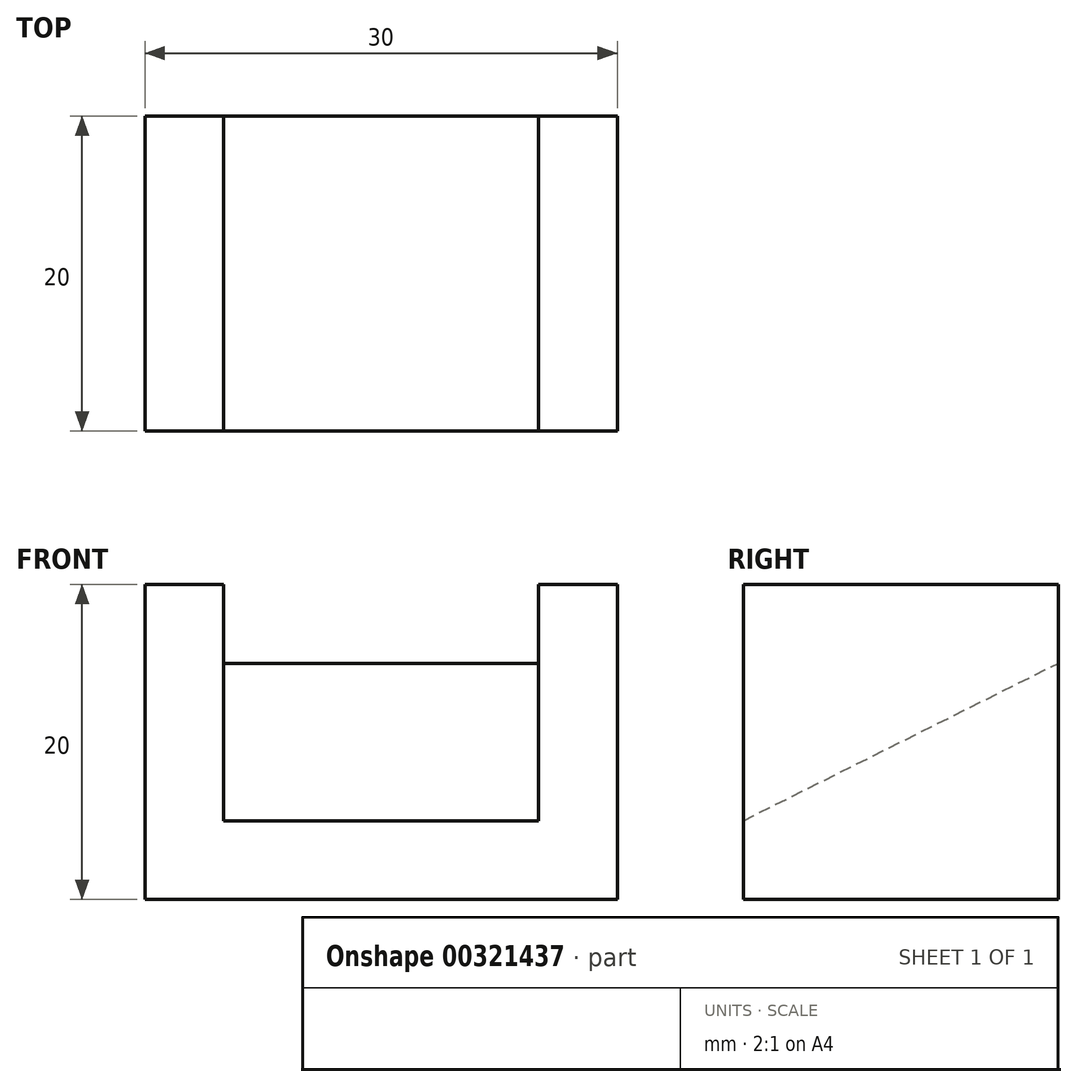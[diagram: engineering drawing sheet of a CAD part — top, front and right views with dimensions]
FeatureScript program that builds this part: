
annotation { "Feature Type Name" : "Feature", "Feature Type Description" : "" }
export const myFeature = defineFeature(function(context is Context, id is Id, definition is map)
    precondition{}
    {
        {
            var Q0;
            Q0=qCreatedBy(makeId("Front.planeOp"),FACE);
            var sketch = newSketch(context, id + "F0", { "sketchPlane" : qUnion([Q0])});
            skLineSegment(sketch, "E0.bottom", {"start": v(0, 0) * mm, "end": v(20, 0) * mm});
            skLineSegment(sketch, "E0.top", {"start": v(0, 15) * mm, "end": v(20, 15) * mm});
            skLineSegment(sketch, "E0.left", {"start": v(0, 0) * mm, "end": v(0, 15) * mm});
            skLineSegment(sketch, "E0.right", {"start": v(20, 0) * mm, "end": v(20, 15) * mm});
            skSolve(sketch);
        }
        {
            var Q0;
            Q0 = qSketchRegion(id + "F0", true);
            extrude(context, id + "F1", {"entities" : qUnion([Q0]), "depth" : 20 * mm});
        }
        {
            var Q0;
            Q0=qCreatedBy(makeId("Right.planeOp"),FACE);
            var sketch = newSketch(context, id + "F2", { "sketchPlane" : qUnion([Q0])});
            skLineSegment(sketch, "E1", {"start": v(-20, 15) * mm, "end": v(-20, 5) * mm});
            skLineSegment(sketch, "E2", {"start": v(-20, 5) * mm, "end": v(0, 15) * mm});
            skLineSegment(sketch, "E3", {"start": v(0, 15) * mm, "end": v(-20, 15) * mm});
            skSolve(sketch);
        }
        {
            var Q0;
            Q0 = qSketchRegion(id + "F2", true);
            extrude(context, id + "F3", {"entities" : qUnion([Q0]), "operationType" : NewBodyOperationType.REMOVE, "endBound" : BoundingType.THROUGH_ALL, "depth" : 25 * mm});
        }
        {
            var Q0;
            Q0=makeQuery(id+"F1.opExtrude","SWEPT_FACE",FACE,{"disambiguationData":[OSD([sQuery(id+"F0.wireOp",EDGE,"E0.right")])]});
            var sketch = newSketch(context, id + "F4", { "sketchPlane" : qUnion([Q0])});
            skLineSegment(sketch, "E4.bottom", {"start": v(0, 0) * mm, "end": v(-20, 0) * mm});
            skLineSegment(sketch, "E4.top", {"start": v(0, 20) * mm, "end": v(-20, 20) * mm});
            skLineSegment(sketch, "E4.left", {"start": v(0, 0) * mm, "end": v(0, 20) * mm});
            skLineSegment(sketch, "E4.right", {"start": v(-20, 0) * mm, "end": v(-20, 20) * mm});
            skSolve(sketch);
        }
        {
            var Q0;
            Q0 = qSketchRegion(id + "F4", true);
            extrude(context, id + "F5", {"entities" : qUnion([Q0]), "operationType" : NewBodyOperationType.ADD, "depth" : 5 * mm});
        }
        {
            var Q0;
            Q0=makeQuery(id+"F1.opExtrude","SWEPT_FACE",FACE,{"disambiguationData":[OSD([sQuery(id+"F0.wireOp",EDGE,"E0.left")])]});
            var sketch = newSketch(context, id + "F6", { "sketchPlane" : qUnion([Q0])});
            skLineSegment(sketch, "E5.bottom", {"start": v(0, 0) * mm, "end": v(20, 0) * mm});
            skLineSegment(sketch, "E5.top", {"start": v(0, 20) * mm, "end": v(20, 20) * mm});
            skLineSegment(sketch, "E5.left", {"start": v(0, 0) * mm, "end": v(0, 20) * mm});
            skLineSegment(sketch, "E5.right", {"start": v(20, 0) * mm, "end": v(20, 20) * mm});
            skSolve(sketch);
        }
        {
            var Q0;
            Q0 = qSketchRegion(id + "F6", true);
            extrude(context, id + "F7", {"entities" : qUnion([Q0]), "operationType" : NewBodyOperationType.ADD, "depth" : 5 * mm});
        }
    });
